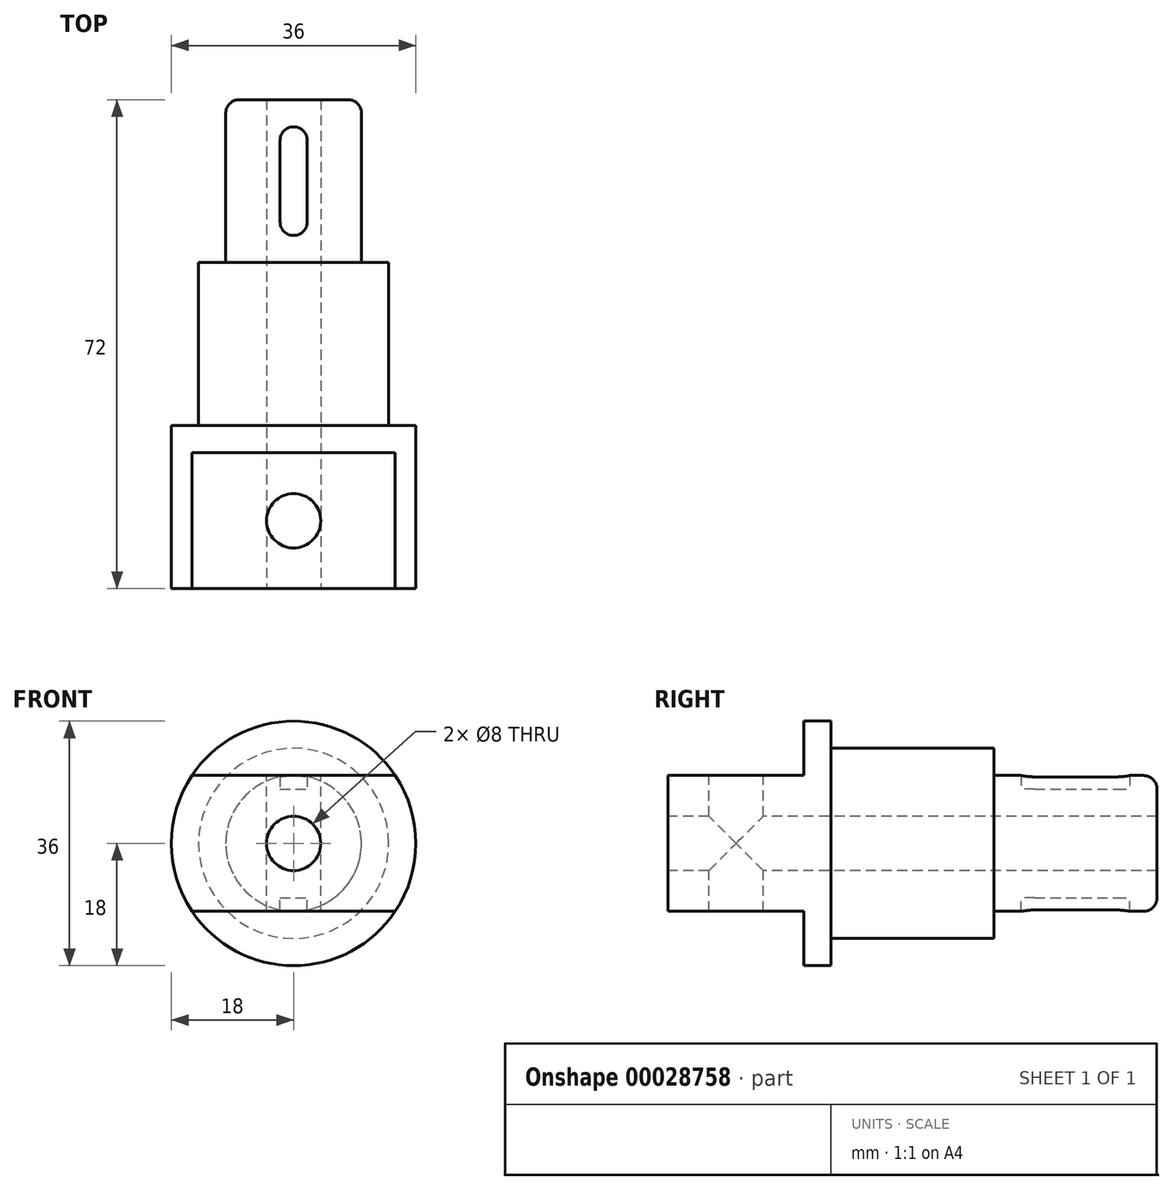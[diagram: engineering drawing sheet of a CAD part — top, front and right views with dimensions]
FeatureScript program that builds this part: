
annotation { "Feature Type Name" : "Feature", "Feature Type Description" : "" }
export const myFeature = defineFeature(function(context is Context, id is Id, definition is map)
    precondition{}
    {
        {
            var Q0;
            Q0=qCreatedBy(makeId("Right.planeOp"),FACE);
            var sketch = newSketch(context, id + "F0", { "sketchPlane" : qUnion([Q0])});
            skLineSegment(sketch, "E0", {"start": v(-159.41, 0) * mm, "end": v(194.23, 0) * mm, "construction": true});
            skLineSegment(sketch, "E1", {"start": v(-72, 18) * mm, "end": v(-48, 18) * mm});
            skLineSegment(sketch, "E2", {"start": v(-48, 18) * mm, "end": v(-48, 14) * mm});
            skLineSegment(sketch, "E3", {"start": v(-48, 14) * mm, "end": v(-24, 14) * mm});
            skLineSegment(sketch, "E4", {"start": v(-24, 14) * mm, "end": v(-24, 10) * mm});
            skLineSegment(sketch, "E5", {"start": v(-24, 10) * mm, "end": v(0, 10) * mm});
            skLineSegment(sketch, "E6", {"start": v(-72, 4) * mm, "end": v(0, 4) * mm});
            skLineSegment(sketch, "E7", {"start": v(-72, 18) * mm, "end": v(-72, 4) * mm});
            skLineSegment(sketch, "E8", {"start": v(0, 10) * mm, "end": v(0, 4) * mm});
            skLineSegment(sketch, "E9", {"start": v(-60, 28.2) * mm, "end": v(-60, -39.18) * mm, "construction": true});
            skPoint(sketch, "E10.endSnap0", {"position": v(-72, 11) * mm});
            skSolve(sketch);
        }
        {
            var Q0;
            Q0=makeQuery(id+"F0.imprint","IMPRINT",FACE,{"disambiguationData":[TD([[makeQuery(id+"F0.imprint","IMPRINT",EDGE,{"derivedFrom":sQuery(id+"F0.wireOp",EDGE,"E1")}),-1.0]])]});
            var Q1;
            Q1=sQuery(id+"F0.wireOp",EDGE,"E0");
            revolve(context, id + "F1", {"entities" : qUnion([Q0]), "axis" : qUnion([Q1]), "revolveType" : RevolveType.FULL});
        }
        {
            var Q0;
            Q0=qCreatedBy(makeId("Top.planeOp"),FACE);
            var sketch = newSketch(context, id + "F2", { "sketchPlane" : qUnion([Q0])});
            skLineSegment(sketch, "E11", {"start": v(0, 0) * mm, "end": v(0, -254.6) * mm, "construction": true});
            skLineSegment(sketch, "E12", {"start": v(35.41, -62) * mm, "end": v(-32.25, -62) * mm, "construction": true});
            skCircle(sketch, "E13", {"center": v(0, -62) * mm, "radius": 4 * mm});
            skLineSegment(sketch, "E14.rect.bottom", {"start": v(18, -72) * mm, "end": v(-18, -72) * mm});
            skLineSegment(sketch, "E14.rect.top", {"start": v(18, -52) * mm, "end": v(-18, -52) * mm});
            skLineSegment(sketch, "E14.rect.left", {"start": v(18, -72) * mm, "end": v(18, -52) * mm});
            skLineSegment(sketch, "E14.rect.right", {"start": v(-18, -72) * mm, "end": v(-18, -52) * mm});
            skLineSegment(sketch, "E15", {"start": v(13.35, -12) * mm, "end": v(-17.63, -12) * mm, "construction": true});
            skLineSegment(sketch, "E16.rect.bottom", {"start": v(0, -4) * mm, "end": v(0, -4) * mm});
            skLineSegment(sketch, "E16.rect.top", {"start": v(0, -20) * mm, "end": v(0, -20) * mm});
            skLineSegment(sketch, "E16.rect.left", {"start": v(2, -6) * mm, "end": v(2, -18) * mm});
            skLineSegment(sketch, "E16.rect.right", {"start": v(-2, -6) * mm, "end": v(-2, -18) * mm});
            skPoint(sketch, "E16.rect.middle", {"position": v(0, -12) * mm});
            skPoint(sketch, "E17.visualSharp", {"position": v(2, -20) * mm});
            skArc(sketch, "E17.filletArc", {"start": v(0, -20) * mm, "mid": v(1.41, -19.41) * mm, "end": v(2, -18) * mm});
            skPoint(sketch, "E18.visualSharp", {"position": v(2, -4) * mm});
            skArc(sketch, "E18.filletArc", {"start": v(2, -6) * mm, "mid": v(1.41, -4.59) * mm, "end": v(0, -4) * mm});
            skPoint(sketch, "E19.visualSharp", {"position": v(-2, -4) * mm});
            skArc(sketch, "E19.filletArc", {"start": v(0, -4) * mm, "mid": v(-1.41, -4.59) * mm, "end": v(-2, -6) * mm});
            skPoint(sketch, "E20.visualSharp", {"position": v(-2, -20) * mm});
            skArc(sketch, "E20.filletArc", {"start": v(-2, -18) * mm, "mid": v(-1.41, -19.41) * mm, "end": v(0, -20) * mm});
            skSolve(sketch);
        }
        {
            var Q0;
            Q0=makeQuery(id+"F2.imprint","IMPRINT",FACE,{"disambiguationData":[TD([[makeQuery(id+"F2.imprint","IMPRINT",EDGE,{"derivedFrom":sQuery(id+"F2.wireOp",EDGE,"E13")}),1.0]])]});
            extrude(context, id + "F3", {"entities" : qUnion([Q0]), "operationType" : NewBodyOperationType.REMOVE, "oppositeDirection" : true, "depth" : 46.87 * mm, "symmetric" : true});
        }
        {
            var Q0;
            Q0=qCreatedBy(makeId("Top.planeOp"),FACE);
            cPlane(context, id + "F4", {"entities" : qUnion([Q0]), "cplaneType" : CPlaneType.OFFSET, "offset" : 10 * mm, "width" : 150 * mm, "height" : 150 * mm});
        }
        {
            var Q0;
            Q0=qCreatedBy(makeId("Top.planeOp"),FACE);
            cPlane(context, id + "F5", {"entities" : qUnion([Q0]), "cplaneType" : CPlaneType.OFFSET, "offset" : 10 * mm, "oppositeDirection" : true, "width" : 150 * mm, "height" : 150 * mm});
        }
        {
            var Q0;
            Q0=qCreatedBy(id+"F5.planeOp",FACE);
            var sketch = newSketch(context, id + "F6", { "sketchPlane" : qUnion([Q0])});
            skLineSegment(sketch, "E21.0", {"start": v(18, -72) * mm, "end": v(-18, -72) * mm});
            skLineSegment(sketch, "E22.0", {"start": v(-18, -72) * mm, "end": v(-18, -52) * mm});
            skLineSegment(sketch, "E23.0", {"start": v(18, -52) * mm, "end": v(-18, -52) * mm});
            skLineSegment(sketch, "E24.0", {"start": v(18, -72) * mm, "end": v(18, -52) * mm});
            skSolve(sketch);
        }
        {
            var Q0;
            Q0=qCreatedBy(id+"F4.planeOp",FACE);
            var sketch = newSketch(context, id + "F7", { "sketchPlane" : qUnion([Q0])});
            skLineSegment(sketch, "E25.0", {"start": v(-18, -72) * mm, "end": v(-18, -52) * mm});
            skLineSegment(sketch, "E25.1", {"start": v(18, -52) * mm, "end": v(-18, -52) * mm});
            skLineSegment(sketch, "E25.2", {"start": v(18, -72) * mm, "end": v(18, -52) * mm});
            skLineSegment(sketch, "E25.3", {"start": v(18, -72) * mm, "end": v(-18, -72) * mm});
            skSolve(sketch);
        }
        {
            var Q0;
            Q0 = qSketchRegion(id + "F6", true);
            extrude(context, id + "F8", {"entities" : qUnion([Q0]), "operationType" : NewBodyOperationType.REMOVE, "oppositeDirection" : true, "depth" : 10 * mm});
        }
        {
            var Q0;
            Q0=makeQuery(id+"F7.imprint","IMPRINT",FACE,{"disambiguationData":[TD([[makeQuery(id+"F7.imprint","IMPRINT",EDGE,{"derivedFrom":sQuery(id+"F7.wireOp",EDGE,"E25.0")}),-1.0]])]});
            extrude(context, id + "F9", {"entities" : qUnion([Q0]), "operationType" : NewBodyOperationType.REMOVE, "depth" : 10 * mm});
        }
        {
            var Q0;
            Q0=qCreatedBy(makeId("Top.planeOp"),FACE);
            cPlane(context, id + "F10", {"entities" : qUnion([Q0]), "cplaneType" : CPlaneType.OFFSET, "offset" : 8 * mm, "width" : 150 * mm, "height" : 150 * mm});
        }
        {
            var Q0;
            Q0=qCreatedBy(makeId("Top.planeOp"),FACE);
            cPlane(context, id + "F11", {"entities" : qUnion([Q0]), "cplaneType" : CPlaneType.OFFSET, "offset" : 8 * mm, "oppositeDirection" : true, "width" : 150 * mm, "height" : 150 * mm});
        }
        {
            var Q0;
            Q0=qCreatedBy(id+"F10.planeOp",FACE);
            var sketch = newSketch(context, id + "F12", { "sketchPlane" : qUnion([Q0])});
            skLineSegment(sketch, "E26.0.0", {"start": v(2, -18) * mm, "end": v(2, -6) * mm});
            skArc(sketch, "E26.0.1", {"start": v(2, -6) * mm, "mid": v(1.41, -4.59) * mm, "end": v(0, -4) * mm});
            skArc(sketch, "E26.0.2", {"start": v(0, -4) * mm, "mid": v(-1.41, -4.59) * mm, "end": v(-2, -6) * mm});
            skLineSegment(sketch, "E26.0.3", {"start": v(-2, -6) * mm, "end": v(-2, -18) * mm});
            skArc(sketch, "E26.0.4", {"start": v(-2, -18) * mm, "mid": v(-1.41, -19.41) * mm, "end": v(0, -20) * mm});
            skArc(sketch, "E26.0.5", {"start": v(0, -20) * mm, "mid": v(1.41, -19.41) * mm, "end": v(2, -18) * mm});
            skSolve(sketch);
        }
        {
            var Q0;
            Q0=qCreatedBy(id+"F11.planeOp",FACE);
            var sketch = newSketch(context, id + "F13", { "sketchPlane" : qUnion([Q0])});
            skLineSegment(sketch, "E27.0.0", {"start": v(2, -18) * mm, "end": v(2, -6) * mm});
            skArc(sketch, "E27.0.1", {"start": v(2, -6) * mm, "mid": v(1.41, -4.59) * mm, "end": v(0, -4) * mm});
            skArc(sketch, "E27.0.2", {"start": v(0, -4) * mm, "mid": v(-1.41, -4.59) * mm, "end": v(-2, -6) * mm});
            skLineSegment(sketch, "E27.0.3", {"start": v(-2, -6) * mm, "end": v(-2, -18) * mm});
            skArc(sketch, "E27.0.4", {"start": v(-2, -18) * mm, "mid": v(-1.41, -19.41) * mm, "end": v(0, -20) * mm});
            skArc(sketch, "E27.0.5", {"start": v(0, -20) * mm, "mid": v(1.41, -19.41) * mm, "end": v(2, -18) * mm});
            skSolve(sketch);
        }
        {
            var Q0;
            Q0 = qSketchRegion(id + "F13", true);
            extrude(context, id + "F14", {"entities" : qUnion([Q0]), "operationType" : NewBodyOperationType.REMOVE, "oppositeDirection" : true, "depth" : 2 * mm});
        }
        {
            var Q0;
            Q0 = qSketchRegion(id + "F12", true);
            extrude(context, id + "F15", {"entities" : qUnion([Q0]), "operationType" : NewBodyOperationType.REMOVE, "depth" : 2 * mm});
        }
        {
            var Q0;
            Q0=makeQuery(id+"F1.opRevolve","SWEPT_EDGE",EDGE,{"disambiguationData":[OSD([sQuery(id+"F0.wireOp",EDGE,"E5"),sQuery(id+"F0.wireOp",EDGE,"E8")])]});
            fillet(context, id + "F16", {"entities" : qUnion([Q0]), "radius" : 2 * mm, "tangentPropagation" : true, "allowEdgeOverflow" : false});
        }
    });
